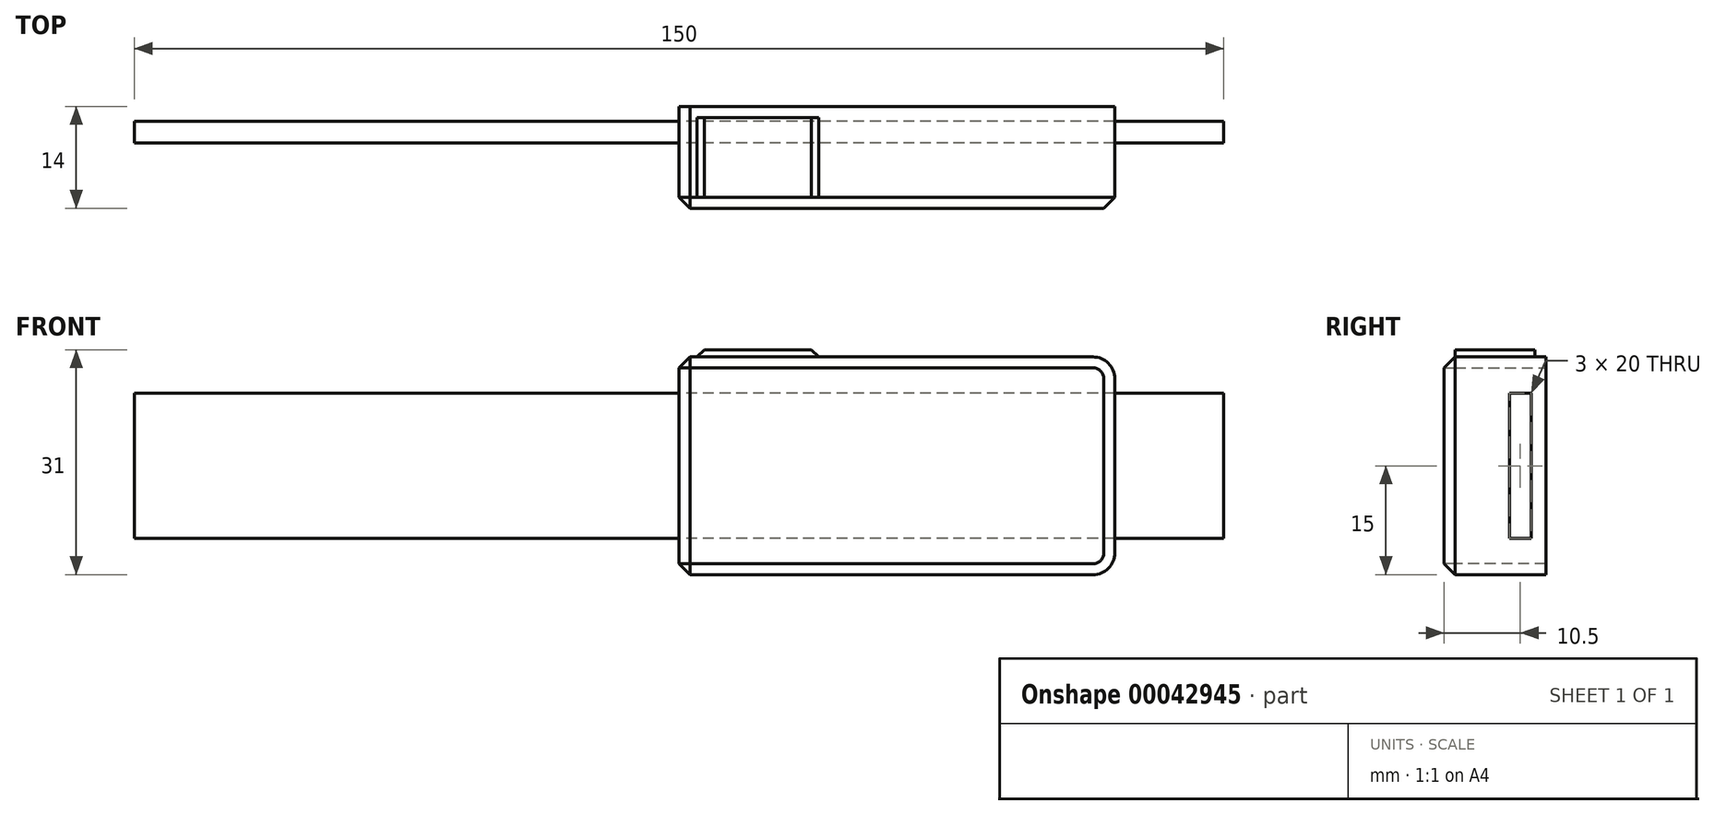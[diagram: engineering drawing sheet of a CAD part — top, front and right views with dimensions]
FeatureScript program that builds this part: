
annotation { "Feature Type Name" : "Feature", "Feature Type Description" : "" }
export const myFeature = defineFeature(function(context is Context, id is Id, definition is map)
    precondition{}
    {
        {
            var Q0;
            Q0=qCreatedBy(makeId("Front.planeOp"),FACE);
            var sketch = newSketch(context, id + "F0", { "sketchPlane" : qUnion([Q0])});
            skLineSegment(sketch, "E0.rect.bottom", {"start": v(30, -15) * mm, "end": v(-30, -15) * mm});
            skLineSegment(sketch, "E0.rect.top", {"start": v(30, 15) * mm, "end": v(-30, 15) * mm});
            skLineSegment(sketch, "E0.rect.left", {"start": v(30, -15) * mm, "end": v(30, 15) * mm});
            skLineSegment(sketch, "E0.rect.right", {"start": v(-30, -15) * mm, "end": v(-30, 15) * mm});
            skPoint(sketch, "E0.rect.middle", {"position": v(0, 0) * mm});
            skSolve(sketch);
        }
        {
            var Q0;
            Q0=makeQuery(id+"F0.imprint","IMPRINT",FACE,{"disambiguationData":[TD([[makeQuery(id+"F0.imprint","IMPRINT",EDGE,{"derivedFrom":sQuery(id+"F0.wireOp",EDGE,"E0.rect.bottom")}),-1.0]])]});
            extrude(context, id + "F1", {"entities" : qUnion([Q0]), "depth" : 14 * mm});
        }
        {
            var Q0;
            Q0=makeQuery(id+"F1.opExtrude","SWEPT_EDGE",EDGE,{"disambiguationData":[OSD([sQuery(id+"F0.wireOp",EDGE,"E0.rect.bottom"),sQuery(id+"F0.wireOp",EDGE,"E0.rect.left")])]});
            var Q1;
            Q1=makeQuery(id+"F1.opExtrude","SWEPT_EDGE",EDGE,{"disambiguationData":[OSD([sQuery(id+"F0.wireOp",EDGE,"E0.rect.top"),sQuery(id+"F0.wireOp",EDGE,"E0.rect.left")])]});
            fillet(context, id + "F2", {"entities" : qUnion([Q0, Q1]), "radius" : 3 * mm, "tangentPropagation" : true, "allowEdgeOverflow" : false});
        }
        {
            var Q0;
            Q0=makeQuery(id+"F1.opExtrude","CAP_EDGE",EDGE,{"disambiguationData":[OSD([sQuery(id+"F0.wireOp",EDGE,"E0.rect.top")])],"isStart":false});
            var Q1;
            {var subQ0=sQuery(id+"F0.wireOp",EDGE,"E0.rect.top");var subQ1=sQuery(id+"F0.wireOp",EDGE,"E0.rect.left");Q1=makeQuery(id+"F2.opFillet","BLEND_EDGE",EDGE,{"blendedFrom":[makeQuery(id+"F1.opExtrude","SWEPT_EDGE",EDGE,{"disambiguationData":[OSD([subQ0,subQ1])]}),makeQuery(id+"F1.opExtrude","CAP_FACE",FACE,{"disambiguationData":[OSD([sQuery(id+"F0.wireOp",EDGE,"E0.rect.bottom"),subQ0,subQ1,sQuery(id+"F0.wireOp",EDGE,"E0.rect.right")])],"isStart":false})],"blendedInto":[makeQuery(id+"F1.opExtrude","CAP_FACE",FACE,{"disambiguationData":[OSD([sQuery(id+"F0.wireOp",EDGE,"E0.rect.bottom"),subQ0,subQ1,sQuery(id+"F0.wireOp",EDGE,"E0.rect.right")])],"isStart":false})]});}
            var Q2;
            Q2=makeQuery(id+"F1.opExtrude","CAP_EDGE",EDGE,{"disambiguationData":[OSD([sQuery(id+"F0.wireOp",EDGE,"E0.rect.left")])],"isStart":false});
            var Q3;
            {var subQ0=sQuery(id+"F0.wireOp",EDGE,"E0.rect.bottom");var subQ1=sQuery(id+"F0.wireOp",EDGE,"E0.rect.left");Q3=makeQuery(id+"F2.opFillet","BLEND_EDGE",EDGE,{"blendedFrom":[makeQuery(id+"F1.opExtrude","SWEPT_EDGE",EDGE,{"disambiguationData":[OSD([subQ0,subQ1])]}),makeQuery(id+"F1.opExtrude","CAP_FACE",FACE,{"disambiguationData":[OSD([subQ0,sQuery(id+"F0.wireOp",EDGE,"E0.rect.top"),subQ1,sQuery(id+"F0.wireOp",EDGE,"E0.rect.right")])],"isStart":false})],"blendedInto":[makeQuery(id+"F1.opExtrude","CAP_FACE",FACE,{"disambiguationData":[OSD([subQ0,sQuery(id+"F0.wireOp",EDGE,"E0.rect.top"),subQ1,sQuery(id+"F0.wireOp",EDGE,"E0.rect.right")])],"isStart":false})]});}
            var Q4;
            Q4=makeQuery(id+"F1.opExtrude","CAP_EDGE",EDGE,{"disambiguationData":[OSD([sQuery(id+"F0.wireOp",EDGE,"E0.rect.bottom")])],"isStart":false});
            var Q5;
            Q5=makeQuery(id+"F1.opExtrude","CAP_EDGE",EDGE,{"disambiguationData":[OSD([sQuery(id+"F0.wireOp",EDGE,"E0.rect.right")])],"isStart":false});
            var Q6;
            Q6=makeQuery(id+"F1.opExtrude","SWEPT_EDGE",EDGE,{"disambiguationData":[OSD([sQuery(id+"F0.wireOp",EDGE,"E0.rect.top"),sQuery(id+"F0.wireOp",EDGE,"E0.rect.right")])]});
            var Q7;
            Q7=makeQuery(id+"F1.opExtrude","SWEPT_EDGE",EDGE,{"disambiguationData":[OSD([sQuery(id+"F0.wireOp",EDGE,"E0.rect.bottom"),sQuery(id+"F0.wireOp",EDGE,"E0.rect.right")])]});
            chamfer(context, id + "F3", {"entities" : qUnion([Q0, Q1, Q2, Q3, Q4, Q5, Q6, Q7]), "width" : 1.5 * mm, "tangentPropagation" : true});
        }
        {
            var Q0;
            Q0=makeQuery(id+"F1.opExtrude","CAP_FACE",FACE,{"disambiguationData":[OSD([sQuery(id+"F0.wireOp",EDGE,"E0.rect.bottom"),sQuery(id+"F0.wireOp",EDGE,"E0.rect.top"),sQuery(id+"F0.wireOp",EDGE,"E0.rect.left"),sQuery(id+"F0.wireOp",EDGE,"E0.rect.right")])],"isStart":false});
            cPlane(context, id + "F4", {"entities" : qUnion([Q0]), "cplaneType" : CPlaneType.OFFSET, "offset" : 1.5 * mm, "oppositeDirection" : true, "width" : 150 * mm, "height" : 150 * mm});
        }
        {
            var Q0;
            Q0=qCreatedBy(id+"F4.planeOp",FACE);
            var sketch = newSketch(context, id + "F5", { "sketchPlane" : qUnion([Q0])});
            skLineSegment(sketch, "E1.0", {"start": v(27, -15) * mm, "end": v(-28.5, -15) * mm});
            skLineSegment(sketch, "E2.0", {"start": v(-28.5, 15) * mm, "end": v(27, 15) * mm});
            skArc(sketch, "E3.0", {"start": v(27, 15) * mm, "mid": v(29.12, 14.12) * mm, "end": v(30, 12) * mm});
            skArc(sketch, "E4.0", {"start": v(30, -12) * mm, "mid": v(29.12, -14.12) * mm, "end": v(27, -15) * mm});
            skLineSegment(sketch, "E5", {"start": v(10.89, -15) * mm, "end": v(14.42, -18.54) * mm});
            skLineSegment(sketch, "E6", {"start": v(20.24, -19.45) * mm, "end": v(27.83, -15.56) * mm});
            skArc(sketch, "E7", {"start": v(27.83, -15.56) * mm, "mid": v(29.41, -14.09) * mm, "end": v(30, -12) * mm});
            skPoint(sketch, "E8.visualSharp", {"position": v(17, -21.11) * mm});
            skArc(sketch, "E8.filletArc", {"start": v(14.42, -18.54) * mm, "mid": v(17.18, -19.94) * mm, "end": v(20.24, -19.45) * mm});
            skLineSegment(sketch, "E9", {"start": v(8.2, -20) * mm, "end": v(32.28, -20) * mm, "construction": true});
            skPoint(sketch, "E10", {"position": v(20.24, -20) * mm});
            skLineSegment(sketch, "E11", {"start": v(10.89, 15) * mm, "end": v(11.89, 16) * mm});
            skLineSegment(sketch, "E12", {"start": v(11.89, 16) * mm, "end": v(26, 16) * mm});
            skArc(sketch, "E13", {"start": v(26, 16) * mm, "mid": v(28.83, 14.83) * mm, "end": v(30, 12) * mm});
            skLineSegment(sketch, "E14", {"start": v(-27.5, 15) * mm, "end": v(-26.5, 16) * mm});
            skLineSegment(sketch, "E15", {"start": v(-26.5, 16) * mm, "end": v(-11.77, 16) * mm});
            skLineSegment(sketch, "E16", {"start": v(-11.77, 16) * mm, "end": v(-10.77, 15) * mm});
            skSolve(sketch);
        }
        {
            var Q0;
            {var subQ2=sQuery(id+"F5.wireOp",EDGE,"E4.0");Q0=makeQuery(id+"F5.imprint","IMPRINT",FACE,{"disambiguationData":[TD([[makeQuery(id+"F5.imprint","IMPRINT",EDGE,{"derivedFrom":subQ2}),1.0]])]});}
            var Q1;
            {var subQ0=sQuery(id+"F5.wireOp",EDGE,"E3.0");Q1=makeQuery(id+"F5.imprint","IMPRINT",FACE,{"disambiguationData":[TD([[makeQuery(id+"F5.imprint","IMPRINT",EDGE,{"derivedFrom":subQ0}),1.0]])]});}
            var Q2;
            {var subQ1=sQuery(id+"F5.wireOp",EDGE,"E14");Q2=makeQuery(id+"F5.imprint","IMPRINT",FACE,{"disambiguationData":[TD([[makeQuery(id+"F5.imprint","IMPRINT",EDGE,{"derivedFrom":subQ1}),-1.0]])]});}
            var Q3;
            Q3=makeQuery(id+"F1.opExtrude","CAP_FACE",FACE,{"disambiguationData":[OSD([sQuery(id+"F0.wireOp",EDGE,"E0.rect.bottom"),sQuery(id+"F0.wireOp",EDGE,"E0.rect.top"),sQuery(id+"F0.wireOp",EDGE,"E0.rect.left"),sQuery(id+"F0.wireOp",EDGE,"E0.rect.right")])],"isStart":true});
            extrude(context, id + "F6", {"entities" : qUnion([Q0, Q1, Q2]), "operationType" : NewBodyOperationType.ADD, "oppositeDirection" : true, "endBoundEntityFace" : qUnion([Q3]), "depth" : 11 * mm});
        }
        {
            var Q0;
            Q0=makeQuery(id+"F1.opExtrude","SWEPT_FACE",FACE,{"disambiguationData":[OSD([sQuery(id+"F0.wireOp",EDGE,"E0.rect.right")])]});
            var sketch = newSketch(context, id + "F7", { "sketchPlane" : qUnion([Q0])});
            skLineSegment(sketch, "E17.0", {"start": v(0, 15) * mm, "end": v(12.5, 15) * mm, "construction": true});
            skLineSegment(sketch, "E18.0", {"start": v(12.5, -15) * mm, "end": v(0, -15) * mm, "construction": true});
            skLineSegment(sketch, "E19.bottom", {"start": v(5, 10) * mm, "end": v(2, 10) * mm});
            skLineSegment(sketch, "E19.top", {"start": v(5, -10) * mm, "end": v(2, -10) * mm});
            skLineSegment(sketch, "E19.left", {"start": v(5, 10) * mm, "end": v(5, -10) * mm});
            skLineSegment(sketch, "E19.right", {"start": v(2, 10) * mm, "end": v(2, -10) * mm});
            skSolve(sketch);
        }
        {
            var Q0;
            Q0=makeQuery(id+"F7.imprint","IMPRINT",FACE,{"disambiguationData":[TD([[makeQuery(id+"F7.imprint","IMPRINT",EDGE,{"derivedFrom":sQuery(id+"F7.wireOp",EDGE,"E19.bottom")}),1.0]])]});
            extrude(context, id + "F8", {"entities" : qUnion([Q0]), "operationType" : NewBodyOperationType.REMOVE, "endBound" : BoundingType.THROUGH_ALL, "oppositeDirection" : true, "depth" : 25 * mm});
        }
        {
            var Q0;
            Q0 = qSketchRegion(id + "F7", true);
            extrude(context, id + "F9", {"entities" : qUnion([Q0]), "endBound" : BoundingType.SYMMETRIC, "depth" : 150 * mm});
        }
        {
            var Q0;
            Q0=makeQuery(id+"F1.opExtrude","CAP_FACE",FACE,{"disambiguationData":[OSD([sQuery(id+"F0.wireOp",EDGE,"E0.rect.bottom"),sQuery(id+"F0.wireOp",EDGE,"E0.rect.top"),sQuery(id+"F0.wireOp",EDGE,"E0.rect.left"),sQuery(id+"F0.wireOp",EDGE,"E0.rect.right")])],"isStart":true});
            var sketch = newSketch(context, id + "F10", { "sketchPlane" : qUnion([Q0])});
            skLineSegment(sketch, "E20.0", {"start": v(105, 10) * mm, "end": v(-45, 10) * mm, "construction": true});
            skPoint(sketch, "E21", {"position": v(30, 1) * mm});
            skSolve(sketch);
        }
    });
